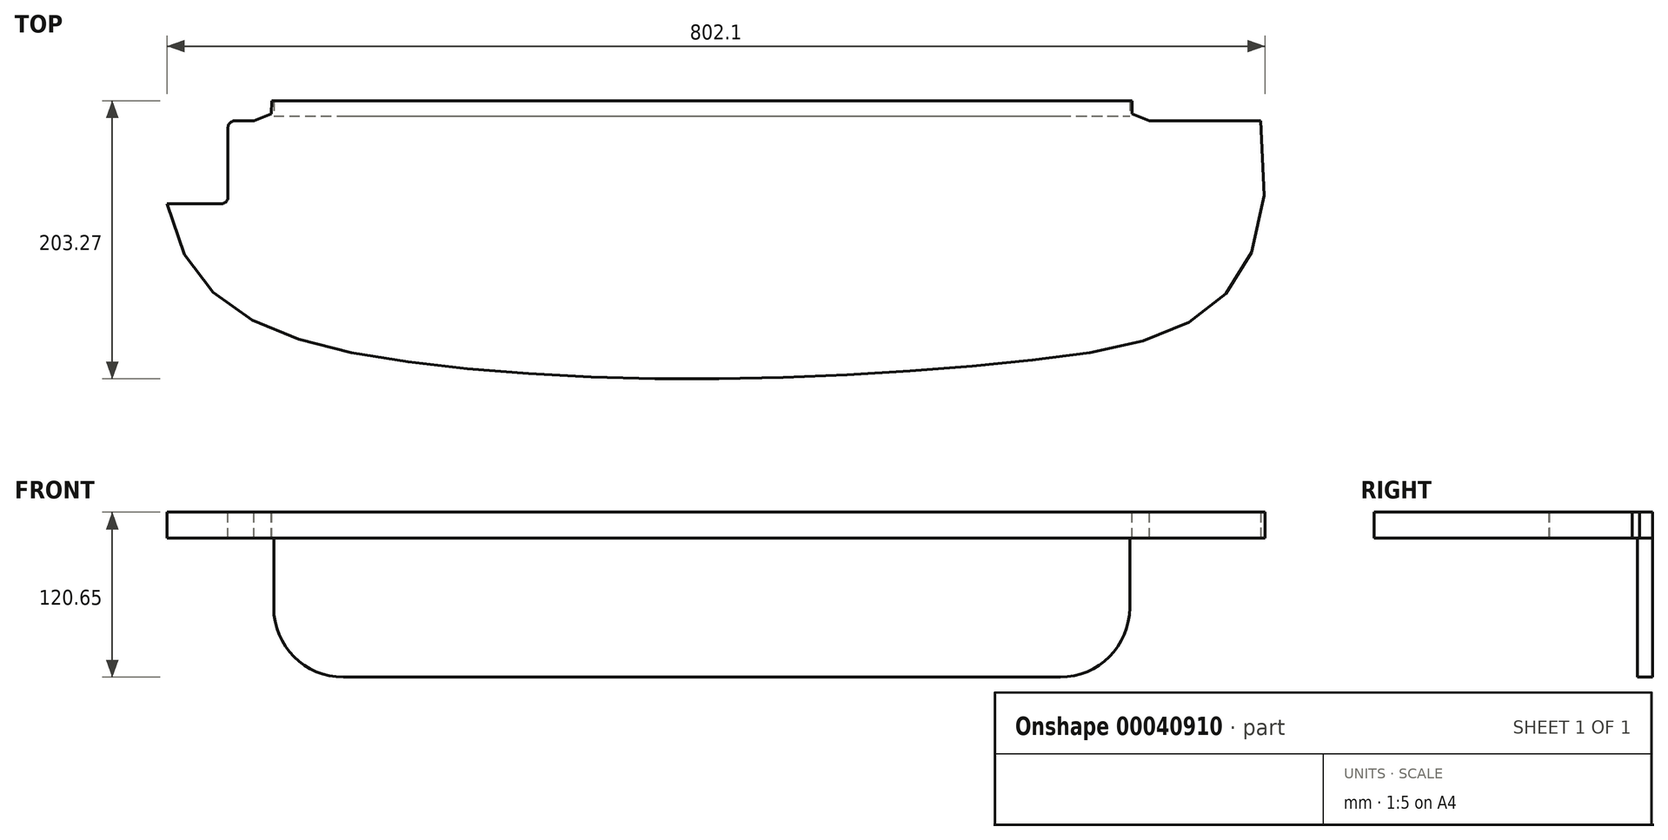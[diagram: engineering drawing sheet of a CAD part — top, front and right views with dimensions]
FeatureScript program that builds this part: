
annotation { "Feature Type Name" : "Feature", "Feature Type Description" : "" }
export const myFeature = defineFeature(function(context is Context, id is Id, definition is map)
    precondition{}
    {
        {
            var Q0;
            Q0=qCreatedBy(makeId("Top.planeOp"),FACE);
            var sketch = newSketch(context, id + "F0", { "sketchPlane" : qUnion([Q0])});
            skFitSpline(sketch, "E0", {"points": [v(-398.46, 0) * mm, v(-224.05, -190.66) * mm, v(224.05, -190.66) * mm, v(398.46, 0) * mm], "startDerivative": vector(-207.75, -1474.6) * mm, "endDerivative": vector(-285.04, 1621.76) * mm, "construction": true});
            skLineSegment(sketch, "E1", {"start": v(0, 517.97) * mm, "end": v(0, -550.45) * mm, "construction": true});
            skLineSegment(sketch, "E2", {"start": v(-398.46, 0) * mm, "end": v(398.46, 0) * mm});
            skPoint(sketch, "E3", {"position": v(0, -203.2) * mm});
            skLineSegment(sketch, "E4", {"start": v(-398.46, 0) * mm, "end": v(-398.46, -75.4) * mm});
            skFitSpline(sketch, "E5", {"points": [v(-398.46, 0) * mm, v(-224.05, -190.66) * mm, v(224.05, -190.66) * mm, v(398.46, 0) * mm], "startDerivative": vector(-207.75, -1474.6) * mm, "endDerivative": vector(-285.04, 1621.76) * mm});
            skSolve(sketch);
        }
        {
            var Q0;
            Q0=makeQuery(id+"F0.imprint","IMPRINT",FACE,{"disambiguationData":[TD([[makeQuery(id+"F0.imprint","IMPRINT",EDGE,{"derivedFrom":sQuery(id+"F0.wireOp",EDGE,"E2")}),-1.0]])]});
            extrude(context, id + "F1", {"entities" : qUnion([Q0]), "depth" : 19.05 * mm});
        }
        {
            var Q0;
            Q0=makeQuery(id+"F1.opExtrude","CAP_FACE",FACE,{"disambiguationData":[OSD([sQuery(id+"F0.wireOp",EDGE,"E2"),sQuery(id+"F0.wireOp",EDGE,"E4"),sQuery(id+"F0.wireOp",EDGE,"E5")])],"isStart":false});
            var sketch = newSketch(context, id + "F2", { "sketchPlane" : qUnion([Q0])});
            skLineSegment(sketch, "E6.bottom", {"start": v(-398.46, 0) * mm, "end": v(-322.13, 0) * mm});
            skLineSegment(sketch, "E6.top", {"start": v(-398.46, -75.4) * mm, "end": v(-354.01, -75.4) * mm});
            skLineSegment(sketch, "E6.left", {"start": v(-398.46, 0) * mm, "end": v(-398.46, -75.4) * mm});
            skLineSegment(sketch, "E7", {"start": v(-354.01, -14.68) * mm, "end": v(-354.01, -75.4) * mm});
            skLineSegment(sketch, "E8", {"start": v(-354.01, -14.68) * mm, "end": v(-334.96, -14.68) * mm});
            skLineSegment(sketch, "E9", {"start": v(-334.96, -14.68) * mm, "end": v(-322.26, -9.52) * mm});
            skLineSegment(sketch, "E10", {"start": v(-322.26, -9.53) * mm, "end": v(-322.13, 0) * mm});
            skLineSegment(sketch, "E11.MirrorCS", {"start": v(-569.33, -65.91) * mm, "end": v(-524.88, -65.91) * mm});
            skLineSegment(sketch, "E12.bottom", {"start": v(-320.54, 0) * mm, "end": v(304.93, 0) * mm, "construction": true});
            skLineSegment(sketch, "E12.top", {"start": v(-320.54, -11.11) * mm, "end": v(304.93, -11.11) * mm, "construction": true});
            skLineSegment(sketch, "E12.left", {"start": v(-320.54, 0) * mm, "end": v(-320.54, -11.11) * mm, "construction": true});
            skLineSegment(sketch, "E12.right", {"start": v(304.93, 0) * mm, "end": v(304.93, -11.11) * mm, "construction": true});
            skPoint(sketch, "E13", {"position": v(-7.8, -11.11) * mm});
            skLineSegment(sketch, "E14", {"start": v(-7.8, 48.66) * mm, "end": v(-7.8, -89.77) * mm, "construction": true});
            skLineSegment(sketch, "E15.MirrorCS", {"start": v(382.86, 0) * mm, "end": v(306.52, 0) * mm});
            skLineSegment(sketch, "E16.MirrorCS", {"start": v(306.66, -9.53) * mm, "end": v(306.52, 0) * mm});
            skLineSegment(sketch, "E17.MirrorCS", {"start": v(319.36, -14.68) * mm, "end": v(306.66, -9.52) * mm});
            skLineSegment(sketch, "E18.MirrorCS", {"start": v(338.4, -14.68) * mm, "end": v(319.36, -14.68) * mm});
            skLineSegment(sketch, "E19", {"start": v(338.4, -14.68) * mm, "end": v(402.68, -14.68) * mm});
            skLineSegment(sketch, "E20", {"start": v(402.68, -14.68) * mm, "end": v(398.46, 0) * mm});
            skLineSegment(sketch, "E21", {"start": v(398.46, 0) * mm, "end": v(382.86, 0) * mm});
            skSolve(sketch);
        }
        {
            var Q0;
            Q0 = qSketchRegion(id + "F2", true);
            extrude(context, id + "F3", {"entities" : qUnion([Q0]), "operationType" : NewBodyOperationType.REMOVE, "oppositeDirection" : true, "depth" : 25.4 * mm});
        }
        {
            var Q0;
            Q0=qCreatedBy(makeId("Top.planeOp"),FACE);
            var sketch = newSketch(context, id + "F4", { "sketchPlane" : qUnion([Q0])});
            skLineSegment(sketch, "E22.bottom", {"start": v(-320.54, 0) * mm, "end": v(304.93, 0) * mm});
            skLineSegment(sketch, "E22.top", {"start": v(-320.54, -11.11) * mm, "end": v(304.93, -11.11) * mm});
            skLineSegment(sketch, "E22.left", {"start": v(-320.54, 0) * mm, "end": v(-320.54, -11.11) * mm});
            skLineSegment(sketch, "E22.right", {"start": v(304.93, 0) * mm, "end": v(304.93, -11.11) * mm});
            skPoint(sketch, "E23", {"position": v(0, 0) * mm});
            skSolve(sketch);
        }
        {
            var Q0;
            Q0 = qSketchRegion(id + "F4", true);
            extrude(context, id + "F5", {"entities" : qUnion([Q0]), "oppositeDirection" : true, "depth" : 101.6 * mm});
        }
        {
            var Q0;
            Q0=makeQuery(id+"F5.opExtrude","CAP_EDGE",EDGE,{"disambiguationData":[OSD([sQuery(id+"F4.wireOp",EDGE,"E22.left")])],"isStart":false});
            var Q1;
            Q1=makeQuery(id+"F5.opExtrude","CAP_EDGE",EDGE,{"disambiguationData":[OSD([sQuery(id+"F4.wireOp",EDGE,"E22.right")])],"isStart":false});
            fillet(context, id + "F6", {"entities" : qUnion([Q0, Q1]), "radius" : 50.8 * mm, "tangentPropagation" : true, "allowEdgeOverflow" : false});
        }
        {
            var Q0;
            Q0=makeQuery(id+"F3.boolean.opBoolean","COPY",EDGE,{"derivedFrom":makeQuery(id+"F3.opExtrude","SWEPT_EDGE",EDGE,{"disambiguationData":[OSD([sQuery(id+"F2.wireOp",EDGE,"E7"),sQuery(id+"F2.wireOp",EDGE,"E11.MirrorCS")])]})});
            fillet(context, id + "F7", {"entities" : qUnion([Q0]), "radius" : 5.08 * mm, "tangentPropagation" : true, "allowEdgeOverflow" : false});
        }
    });
